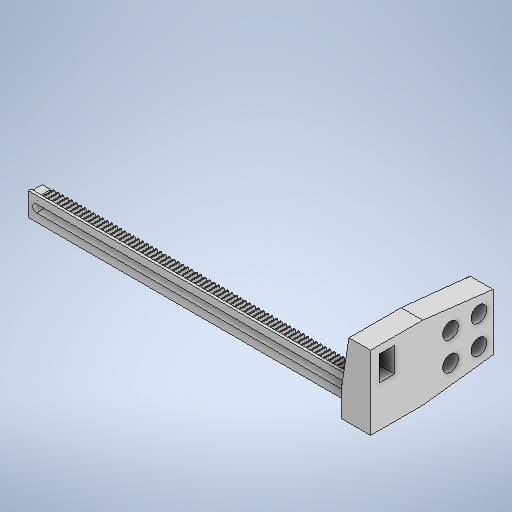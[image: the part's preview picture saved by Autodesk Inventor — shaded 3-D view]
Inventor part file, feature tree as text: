
AUTODESK INVENTOR PART (.ipt)
format: ipt  version: 2025.1 (Build 291241000, 241)  size: 1,878,016 bytes
history: native  units: mm
features: sketch x17, extrude x16, projected_geometry x8, chamfer x4, plane x1
ambient origin geometry x8: Origin, YZ Plane, XZ Plane, XY Plane, X Axis, Y Axis, Z Axis, Center Point
bodies: Solid1 (feature_tree)
feature tree (46):
  extrude  "Extrusion1"  Depth=0.785398mm
  extrude  "Extrusion2"  Depth=0.5mm
  chamfer  "Chamfer1"  Distance=5.0mm
  chamfer  "Chamfer2"  Distance=7.0mm
  sketch  "Sketch3"  dims[d7=0.25mm]
  extrude  "Extrusion3"  Depth=14.0mm TaperAngle=45.0deg
  extrude  "Extrusion4"  Depth=3.0mm
  extrude  "Extrusion5"  Depth=3.0mm
  extrude  "Extrusion6"  Depth=3.0mm TaperAngle=0.0deg
  extrude  "Extrusion7"  Depth=3.0mm
  extrude  "Extrusion8"  Depth=3.0mm
  extrude  "Extrusion9"  Depth=3.0mm
  extrude  "Extrusion10"  Depth=3.0mm TaperAngle=0.0deg
  extrude  "Extrusion11"  Depth=3.0mm
  chamfer  "Chamfer3"  Distance=10.0mm
  extrude  "Extrusion12"  Depth=3.0mm TaperAngle=0.0deg
  extrude  "Extrusion13"  Depth=3.0mm TaperAngle=0.0deg
  extrude  "Extrusion14"  Depth=3.0mm
  chamfer  "Chamfer4"  Distance=3.0mm
  extrude  "Extrusion15"  TaperAngle=0.0deg  [1 undecoded]
  extrude  "Extrusion16"  Depth=3.0mm TaperAngle=0.0deg
  plane  "Work Plane2"
  sketch  "Sketch1"  dims[d1=0.785398mm d2=0.785398mm]
  sketch  "Sketch2"  dims[d3=1.570796mm d5=0.5mm]
  projected_geometry  "Projected Loop1"
  sketch  "Sketch Rectangular Pattern2"  dims[d6=12.217305mm]
  projected_geometry  "Projected Loop2"
  sketch  "Sketch4"  dims[d16=3.0mm]
  sketch  "Sketch5"  dims[d20=115.955743mm d22=5.0mm d23=0.0mm]
  projected_geometry  "Projected Loop3"
  sketch  "Sketch6"  dims[d24=40.0mm]
  projected_geometry  "Projected Loop4"
  sketch  "Sketch7"  dims[d25=20.0mm]
  projected_geometry  "Projected Loop5"
  sketch  "Sketch10"  dims[d26=10.0mm]
  sketch  "Sketch11"  dims[d27=5.0mm]
  sketch  "Sketch12"  dims[d28=10.0mm]
  sketch  "Sketch13"  dims[d29=5.0mm]
  sketch  "Sketch14"  dims[d30=5.6mm]
  sketch  "Sketch16"  dims[d31=20.0mm d33=10.0mm d34=20.0mm d36=10.0mm d39=7.0mm d40=0.0mm]
  projected_geometry  "Projected Loop6"
  sketch  "Sketch17"  dims[d42=12.4999mm d43=2.0mm d44=45.0deg d45=14.0mm d46=2.0mm d47=45.0deg]
  projected_geometry  "Projected Loop7"
  sketch  "Sketch18"  dims[d48=2.7mm d49=3.0mm d50=3.0mm d51=7.0mm d52=0.0mm d53=10.0mm d54=11.5mm d55=0.5mm d56=0.3mm d57=0.0mm d58=8.2mm d59=10.0mm d60=0.0mm d61=0.2mm d62=0.0mm d63=0.2mm d64=0.0mm d65=3.0mm d66=3.0mm d67=0.0mm d68=0.0mm d69=0.0mm d70=10.0mm d71=0.0mm d72=10.0mm d73=0.0mm d74=24.8mm d75=3.0mm d76=45.0deg d77=0.25mm d78=0.0mm d79=0.2mm d80=0.0mm d81=1.0mm d82=0.0mm d86=18.4mm d87=3.0mm d88=0.0mm d89=24.8mm d90=3.0mm d91=45.0deg d92=0.5mm d93=1.1mm d94=0.0mm d95=0.3mm d96=0.0mm d97=700.0mm d99=1.570796mm d100=10.0mm d102=10.0mm d104=3.0mm d105=7.5mm]
  projected_geometry  "Projected Loop8"
  sketch  "Sketch Rectangular Pattern3"  dims[d8=0.1mm]
note: 1 required parameter value undecoded (feature->parameter linkage not recoverable at this tier; creation-order binding heuristic only, values carry confidence <= 0.55)
